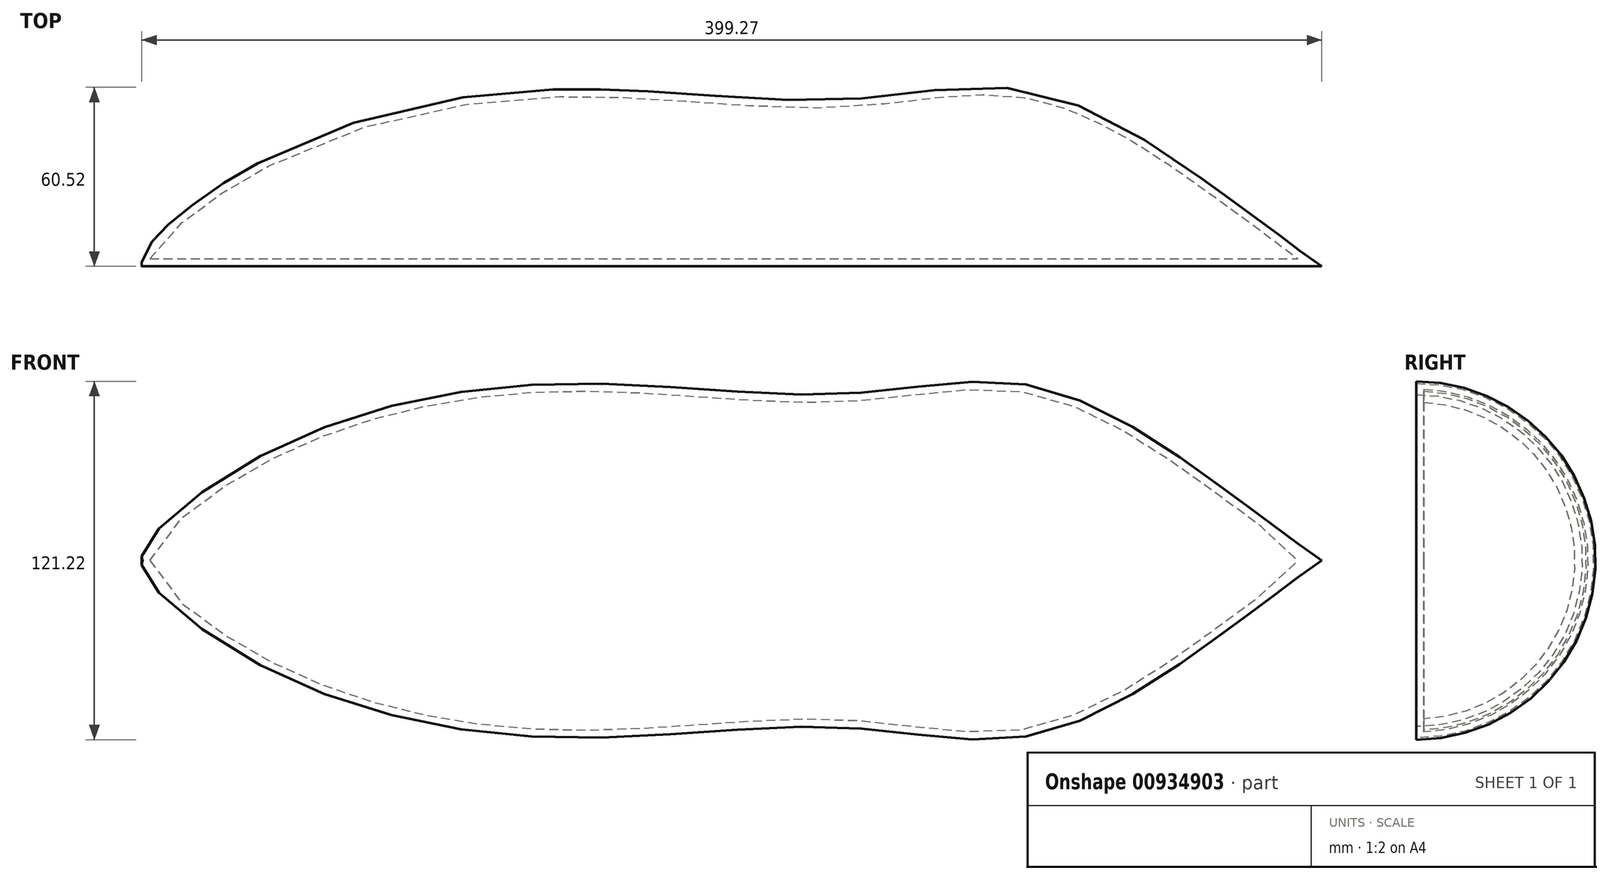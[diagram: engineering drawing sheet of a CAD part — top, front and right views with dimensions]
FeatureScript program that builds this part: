
annotation { "Feature Type Name" : "Feature", "Feature Type Description" : "" }
export const myFeature = defineFeature(function(context is Context, id is Id, definition is map)
    precondition{}
    {
        {
            var Q0;
            Q0=qCreatedBy(makeId("Top.planeOp"),FACE);
            var sketch = newSketch(context, id + "F0", { "sketchPlane" : qUnion([Q0])});
            skLineSegment(sketch, "E0", {"start": v(0, 0) * mm, "end": v(-398.92, 0) * mm});
            skFitSpline(sketch, "E1", {"points": [v(-398.92, 0) * mm, v(-361.73, 33.93) * mm, v(-257.89, 59.9) * mm, v(-162.18, 56.38) * mm, v(-95.44, 58.64) * mm, v(-37.08, 27.15) * mm, v(-16.35, 11.95) * mm, v(0, 0) * mm], "startDerivative": vector(-70.2, 131.02) * mm, "endDerivative": vector(186.74, -123.64) * mm});
            skSolve(sketch);
        }
        {
            var Q0;
            Q0=makeQuery(id+"F0.imprint","IMPRINT",FACE,{"disambiguationData":[TD([[makeQuery(id+"F0.imprint","IMPRINT",EDGE,{"derivedFrom":sQuery(id+"F0.wireOp",EDGE,"E0")}),-1.0]])]});
            var Q1;
            Q1=sQuery(id+"F0.wireOp",EDGE,"E0");
            revolve(context, id + "F1", {"surfaceOperationType" : NewSurfaceOperationType.NEW, "entities" : qUnion([Q0]), "axis" : qUnion([Q1]), "revolveType" : RevolveType.SYMMETRIC, "angle" : 180 * degree});
        }
        {
            var Q0;
            Q0=makeQuery(id+"F1.opRevolve","CAP_FACE",FACE,{"disambiguationData":[OSD([sQuery(id+"F0.wireOp",EDGE,"E0"),sQuery(id+"F0.wireOp",EDGE,"E1")])],"isStart":true});
            var Q1;
            Q1=makeQuery(id+"F1.opRevolve","SWEPT_BODY",BODY,{"disambiguationData":[OSD([sQuery(id+"F0.wireOp",EDGE,"E0"),sQuery(id+"F0.wireOp",EDGE,"E1")])]});
            shell(context, id + "F2", {"isHollow" : true, "entities" : qUnion([Q0]), "parts" : qUnion([Q1]), "thickness" : 2.54 * mm});
        }
    });
